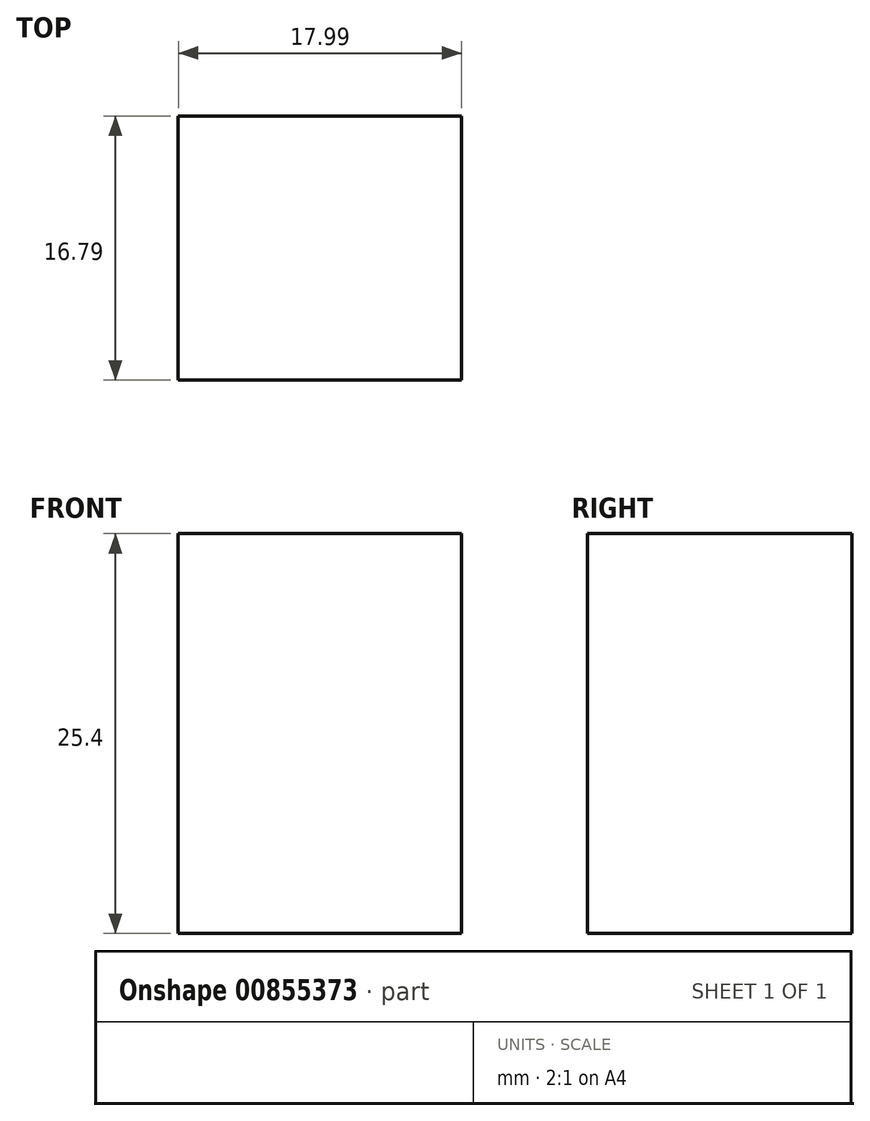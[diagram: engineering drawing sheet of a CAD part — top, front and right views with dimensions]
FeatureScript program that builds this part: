
annotation { "Feature Type Name" : "Feature", "Feature Type Description" : "" }
export const myFeature = defineFeature(function(context is Context, id is Id, definition is map)
    precondition{}
    {
        {
            var Q0;
            Q0=qCreatedBy(makeId("Top.planeOp"),FACE);
            var sketch = newSketch(context, id + "F0", { "sketchPlane" : qUnion([Q0])});
            skLineSegment(sketch, "E0", {"start": v(0, 0) * mm, "end": v(0, 18.42) * mm});
            skLineSegment(sketch, "E1", {"start": v(0, 18.42) * mm, "end": v(21.1, 18.42) * mm});
            skLineSegment(sketch, "E2", {"start": v(21.1, 18.42) * mm, "end": v(21.1, 0) * mm});
            skLineSegment(sketch, "E3.bottom", {"start": v(-22.5, 1.13) * mm, "end": v(-40.48, 1.13) * mm});
            skLineSegment(sketch, "E3.top", {"start": v(-22.5, 17.92) * mm, "end": v(-40.48, 17.92) * mm});
            skLineSegment(sketch, "E3.left", {"start": v(-22.5, 1.13) * mm, "end": v(-22.5, 17.92) * mm});
            skLineSegment(sketch, "E3.right", {"start": v(-40.48, 1.13) * mm, "end": v(-40.48, 17.92) * mm});
            skSolve(sketch);
        }
        {
            var Q0;
            Q0=makeQuery(id+"F0.imprint","IMPRINT",FACE,{"disambiguationData":[TD([[makeQuery(id+"F0.imprint","IMPRINT",EDGE,{"derivedFrom":sQuery(id+"F0.wireOp",EDGE,"E3.bottom")}),-1.0]])]});
            extrude(context, id + "F1", {"entities" : qUnion([Q0]), "depth" : 25.4 * mm, "offsetDistance" : 25.4 * mm});
        }
    });
